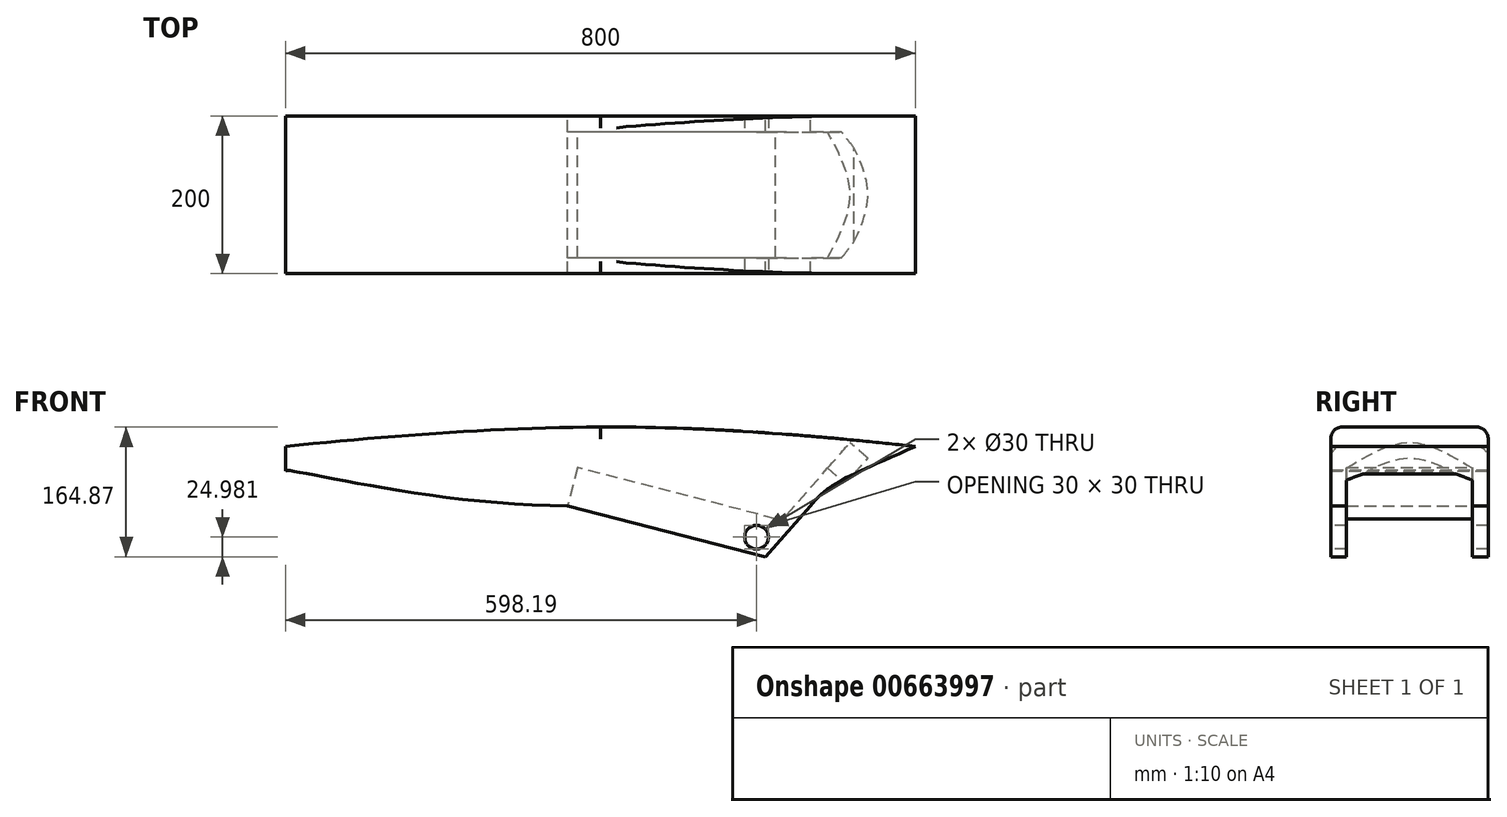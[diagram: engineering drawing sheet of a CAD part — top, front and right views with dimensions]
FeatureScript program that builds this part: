
annotation { "Feature Type Name" : "Feature", "Feature Type Description" : "" }
export const myFeature = defineFeature(function(context is Context, id is Id, definition is map)
    precondition{}
    {
        {
            var Q0;
            Q0=qCreatedBy(makeId("Front.planeOp"),FACE);
            var sketch = newSketch(context, id + "F0", { "sketchPlane" : qUnion([Q0])});
            skLineSegment(sketch, "E0.bottom", {"start": v(400, 100) * mm, "end": v(-400, 100) * mm});
            skLineSegment(sketch, "E0.top", {"start": v(400, -100) * mm, "end": v(-400, -100) * mm});
            skLineSegment(sketch, "E0.left", {"start": v(400, 100) * mm, "end": v(400, -100) * mm});
            skLineSegment(sketch, "E0.right", {"start": v(-400, 100) * mm, "end": v(-400, -100) * mm});
            skPoint(sketch, "E0.middle", {"position": v(0, 0) * mm});
            skFitSpline(sketch, "E1", {"points": [v(-400, 75.5) * mm, v(0, 100) * mm, v(400, 75.5) * mm], "startDerivative": vector(748.06, 77.9) * mm, "endDerivative": vector(850.47, -90.52) * mm});
            skLineSegment(sketch, "E2", {"start": v(400, 75.5) * mm, "end": v(-400, 75.5) * mm, "construction": true});
            skFitSpline(sketch, "E3", {"points": [v(400, 75.5) * mm, v(266.67, 0) * mm], "startDerivative": vector(-259.24, -116.65) * mm, "endDerivative": vector(-73.72, -89.73) * mm});
            skLineSegment(sketch, "E4", {"start": v(266.67, 0) * mm, "end": v(209.84, -64.87) * mm});
            skLineSegment(sketch, "E5", {"start": v(209.84, -64.87) * mm, "end": v(-41.63, 0) * mm});
            skFitSpline(sketch, "E6", {"points": [v(-41.63, 0) * mm, v(-400, 44.43) * mm, v(-400, 43.31) * mm], "startDerivative": vector(-547.86, 0) * mm, "endDerivative": vector(9.97, -23) * mm});
            skSolve(sketch);
        }
        {
            var Q0;
            {var subQ5=sQuery(id+"F0.wireOp",EDGE,"E3");Q0=makeQuery(id+"F0.imprint","IMPRINT",FACE,{"disambiguationData":[TD([[makeQuery(id+"F0.imprint","IMPRINT",EDGE,{"derivedFrom":subQ5}),-1.0]])]});}
            extrude(context, id + "F1", {"entities" : qUnion([Q0]), "depth" : 200 * mm, "offsetDistance" : 25 * mm});
        }
        {
            var Q0;
            {var subQ0=sQuery(id+"F0.wireOp",EDGE,"E1");Q0=makeQuery(id+"F1.opExtrude","CAP_EDGE",EDGE,{"disambiguationData":[OSD([subQ0]),TDD([makeQuery(id+"F0.imprint","IMPRINT",EDGE,{"disambiguationData":[TD([[makeQuery(id+"F0.imprint","INTERSECT",VERTEX,{"derivedFrom":[sQuery(id+"F0.wireOp",EDGE,"E0.right"),subQ0]}),-1.0]])],"derivedFrom":subQ0})])],"isStart":false});}
            var Q1;
            {var subQ0=sQuery(id+"F0.wireOp",EDGE,"E1");Q1=makeQuery(id+"F1.opExtrude","CAP_EDGE",EDGE,{"disambiguationData":[OSD([subQ0]),TDD([makeQuery(id+"F0.imprint","IMPRINT",EDGE,{"disambiguationData":[TD([[makeQuery(id+"F0.imprint","INTERSECT",VERTEX,{"disambiguationData":[OD(0.0)],"derivedFrom":[sQuery(id+"F0.wireOp",EDGE,"E0.bottom"),subQ0]}),-1.0]])],"derivedFrom":subQ0})])],"isStart":false});}
            var Q2;
            {var subQ0=sQuery(id+"F0.wireOp",EDGE,"E1");Q2=makeQuery(id+"F1.opExtrude","CAP_EDGE",EDGE,{"disambiguationData":[OSD([subQ0]),TDD([makeQuery(id+"F0.imprint","IMPRINT",EDGE,{"disambiguationData":[TD([[makeQuery(id+"F0.imprint","INTERSECT",VERTEX,{"derivedFrom":[sQuery(id+"F0.wireOp",EDGE,"E0.right"),subQ0]}),-1.0]])],"derivedFrom":subQ0})])],"isStart":true});}
            var Q3;
            Q3=makeQuery(id+"F1.opExtrude","CAP_EDGE",EDGE,{"disambiguationData":[OSD([sQuery(id+"F0.wireOp",EDGE,"E0.bottom")])],"isStart":false});
            var Q4;
            Q4=makeQuery(id+"F1.opExtrude","CAP_EDGE",EDGE,{"disambiguationData":[OSD([sQuery(id+"F0.wireOp",EDGE,"E0.bottom")])],"isStart":true});
            var Q5;
            {var subQ0=sQuery(id+"F0.wireOp",EDGE,"E1");Q5=makeQuery(id+"F1.opExtrude","CAP_EDGE",EDGE,{"disambiguationData":[OSD([subQ0]),TDD([makeQuery(id+"F0.imprint","IMPRINT",EDGE,{"disambiguationData":[TD([[makeQuery(id+"F0.imprint","INTERSECT",VERTEX,{"disambiguationData":[OD(0.0)],"derivedFrom":[sQuery(id+"F0.wireOp",EDGE,"E0.bottom"),subQ0]}),-1.0]])],"derivedFrom":subQ0})])],"isStart":true});}
            fillet(context, id + "F2", {"entities" : qUnion([Q0, Q1, Q2, Q3, Q4, Q5]), "radius" : 15 * mm, "tangentPropagation" : true, "allowEdgeOverflow" : false});
        }
        {
            var Q0;
            Q0=makeQuery(id+"F1.opExtrude","SWEPT_FACE",FACE,{"disambiguationData":[OSD([sQuery(id+"F0.wireOp",EDGE,"E4")])]});
            var sketch = newSketch(context, id + "F3", { "sketchPlane" : qUnion([Q0])});
            skLineSegment(sketch, "E7", {"start": v(-100, 320.37) * mm, "end": v(-100, 89.49) * mm, "construction": true});
            skLineSegment(sketch, "E8", {"start": v(-180, 89.49) * mm, "end": v(-180, 226.17) * mm});
            skLineSegment(sketch, "E9.MirrorCS", {"start": v(-20, 89.49) * mm, "end": v(-20, 226.17) * mm});
            skFitSpline(sketch, "E10", {"points": [v(-180, 226.17) * mm, v(-100, 269.31) * mm, v(-20, 226.17) * mm], "startDerivative": vector(160, 129.43) * mm, "endDerivative": vector(160, -129.43) * mm});
            skLineSegment(sketch, "E11", {"start": v(-180, 89.49) * mm, "end": v(-20, 89.49) * mm});
            skSolve(sketch);
        }
        {
            var Q0;
            Q0 = qSketchRegion(id + "F3", true);
            extrude(context, id + "F4", {"entities" : qUnion([Q0]), "operationType" : NewBodyOperationType.REMOVE, "endBound" : BoundingType.SYMMETRIC, "oppositeDirection" : true, "depth" : 30 * mm, "offsetDistance" : 25 * mm});
        }
        {
            var Q0;
            Q0=makeQuery(id+"F1.opExtrude","SWEPT_FACE",FACE,{"disambiguationData":[OSD([sQuery(id+"F0.wireOp",EDGE,"E5")])]});
            var sketch = newSketch(context, id + "F5", { "sketchPlane" : qUnion([Q0])});
            skLineSegment(sketch, "E12", {"start": v(219.4, 180) * mm, "end": v(-40.3, 180) * mm});
            skLineSegment(sketch, "E13", {"start": v(219.4, 20) * mm, "end": v(-40.3, 20) * mm});
            skLineSegment(sketch, "E14", {"start": v(-40.3, 20) * mm, "end": v(-40.3, 180) * mm});
            skSolve(sketch);
        }
        {
            var Q0;
            Q0 = qSketchRegion(id + "F5", true);
            var Q1;
            Q1=makeQuery(id+"F5.imprint","IMPRINT",FACE,{"disambiguationData":[TD([[makeQuery(id+"F5.imprint","IMPRINT",EDGE,{"derivedFrom":sQuery(id+"F5.wireOp",EDGE,"E12")}),1.0]])]});
            extrude(context, id + "F6", {"entities" : qUnion([Q0, Q1]), "operationType" : NewBodyOperationType.REMOVE, "oppositeDirection" : true, "depth" : 50 * mm, "offsetDistance" : 25 * mm});
        }
        {
            var Q0;
            Q0=makeQuery(id+"F6.boolean.opBoolean","INTERSECT",EDGE,{"derivedFrom":[makeQuery(id+"F4.boolean.opBoolean","COPY",FACE,{"derivedFrom":makeQuery(id+"F4.opExtrude","CAP_FACE",FACE,{"disambiguationData":[OSD([sQuery(id+"F3.wireOp",EDGE,"E8"),sQuery(id+"F3.wireOp",EDGE,"E9.MirrorCS"),sQuery(id+"F3.wireOp",EDGE,"E10"),sQuery(id+"F3.wireOp",EDGE,"E11")])],"isStart":false})}),makeQuery(id+"F6.opExtrude","SWEPT_FACE",FACE,{"disambiguationData":[OSD([sQuery(id+"F0.wireOp",EDGE,"E4"),sQuery(id+"F0.wireOp",EDGE,"E5")])]})]});
            fillet(context, id + "F7", {"entities" : qUnion([Q0]), "radius" : 15 * mm, "tangentPropagation" : true, "allowEdgeOverflow" : false});
        }
        {
            var Q0;
            Q0=makeQuery(id+"F1.opExtrude","CAP_FACE",FACE,{"disambiguationData":[OSD([sQuery(id+"F0.wireOp",EDGE,"E0.bottom"),sQuery(id+"F0.wireOp",EDGE,"E0.right"),sQuery(id+"F0.wireOp",EDGE,"E1"),sQuery(id+"F0.wireOp",EDGE,"E3"),sQuery(id+"F0.wireOp",EDGE,"E4"),sQuery(id+"F0.wireOp",EDGE,"E5"),sQuery(id+"F0.wireOp",EDGE,"E6")])],"isStart":false});
            var sketch = newSketch(context, id + "F8", { "sketchPlane" : qUnion([Q0])});
            skCircle(sketch, "E15", {"center": v(198.2, -39.89) * mm, "radius": 15 * mm});
            skSolve(sketch);
        }
        {
            var Q0;
            Q0 = qSketchRegion(id + "F8", true);
            extrude(context, id + "F9", {"entities" : qUnion([Q0]), "operationType" : NewBodyOperationType.REMOVE, "oppositeDirection" : true, "depth" : 300 * mm, "offsetDistance" : 25 * mm});
        }
    });
